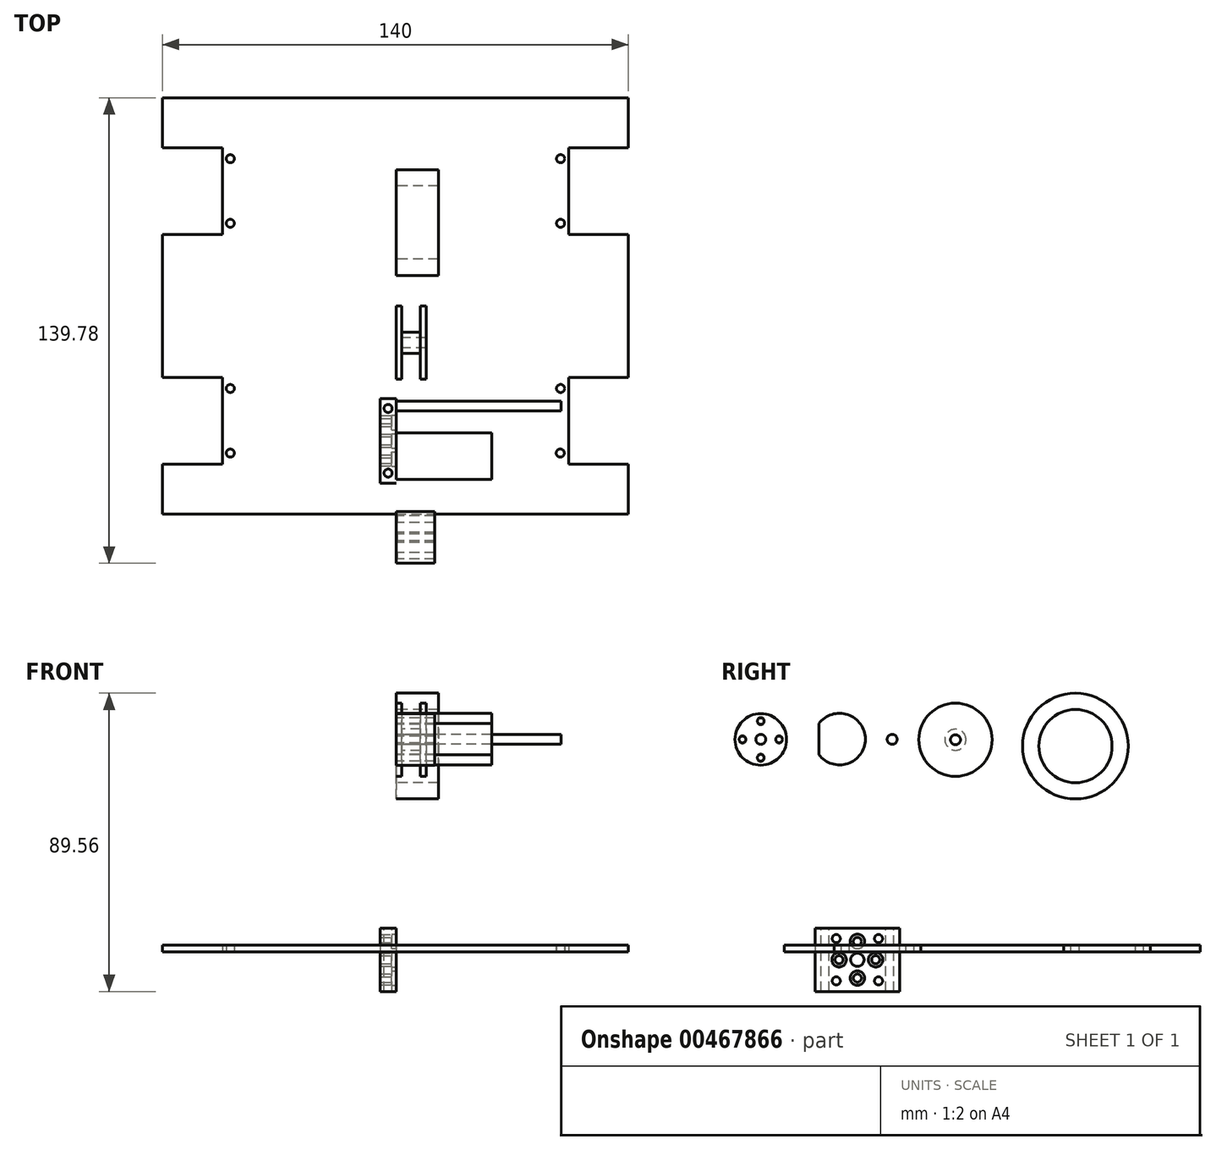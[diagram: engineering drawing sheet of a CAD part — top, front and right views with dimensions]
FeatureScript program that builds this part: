
annotation { "Feature Type Name" : "Feature", "Feature Type Description" : "" }
export const myFeature = defineFeature(function(context is Context, id is Id, definition is map)
    precondition{}
    {
        {
            var Q0;
            Q0=qCreatedBy(makeId("Top.planeOp"),FACE);
            var sketch = newSketch(context, id + "F0", { "sketchPlane" : qUnion([Q0])});
            skLineSegment(sketch, "E0.top", {"start": v(69.81, 68.61) * mm, "end": v(-70.19, 68.61) * mm});
            skPoint(sketch, "E0.middle", {"position": v(-0.01, 0) * mm});
            skLineSegment(sketch, "E1", {"start": v(69.81, 53.61) * mm, "end": v(69.81, 68.61) * mm});
            skLineSegment(sketch, "E2", {"start": v(-70.19, 53.61) * mm, "end": v(-52.19, 53.61) * mm});
            skLineSegment(sketch, "E3", {"start": v(-52.19, 27.61) * mm, "end": v(-52.19, 53.61) * mm});
            skLineSegment(sketch, "E4", {"start": v(-70.19, 53.61) * mm, "end": v(-70.19, 68.61) * mm});
            skLineSegment(sketch, "E5", {"start": v(-52.19, 27.61) * mm, "end": v(-70.19, 27.61) * mm});
            skLineSegment(sketch, "E6", {"start": v(-70.19, -56.39) * mm, "end": v(69.81, -56.39) * mm});
            skLineSegment(sketch, "E7", {"start": v(69.81, 53.61) * mm, "end": v(51.81, 53.61) * mm});
            skLineSegment(sketch, "E8", {"start": v(51.81, 53.61) * mm, "end": v(51.81, 27.61) * mm});
            skLineSegment(sketch, "E9", {"start": v(51.81, 27.61) * mm, "end": v(69.81, 27.61) * mm});
            skLineSegment(sketch, "E10", {"start": v(69.81, -56.39) * mm, "end": v(69.81, -41.39) * mm});
            skLineSegment(sketch, "E11", {"start": v(69.81, -41.39) * mm, "end": v(51.81, -41.39) * mm});
            skLineSegment(sketch, "E12", {"start": v(51.81, -41.39) * mm, "end": v(51.81, -15.39) * mm});
            skLineSegment(sketch, "E13", {"start": v(51.81, -15.39) * mm, "end": v(69.81, -15.39) * mm});
            skLineSegment(sketch, "E14", {"start": v(-70.19, -56.39) * mm, "end": v(-70.19, -41.39) * mm});
            skLineSegment(sketch, "E15", {"start": v(-70.19, -41.39) * mm, "end": v(-52.19, -41.39) * mm});
            skLineSegment(sketch, "E16", {"start": v(-52.19, -41.39) * mm, "end": v(-52.19, -15.39) * mm});
            skLineSegment(sketch, "E17", {"start": v(-52.19, -15.39) * mm, "end": v(-70.19, -15.39) * mm});
            skLineSegment(sketch, "E18", {"start": v(-70.19, 27.61) * mm, "end": v(-70.19, -15.39) * mm});
            skLineSegment(sketch, "E19", {"start": v(69.81, 27.61) * mm, "end": v(69.81, -15.39) * mm});
            skCircle(sketch, "E20", {"center": v(-49.8, -18.69) * mm, "radius": 1.22 * mm});
            skCircle(sketch, "E21", {"center": v(-49.8, -38.09) * mm, "radius": 1.22 * mm});
            skCircle(sketch, "E22", {"center": v(49.43, -18.69) * mm, "radius": 1.22 * mm});
            skCircle(sketch, "E23", {"center": v(49.33, -38.09) * mm, "radius": 1.22 * mm});
            skCircle(sketch, "E24", {"center": v(49.43, 50.31) * mm, "radius": 1.22 * mm});
            skCircle(sketch, "E25", {"center": v(49.43, 30.91) * mm, "radius": 1.22 * mm});
            skCircle(sketch, "E26", {"center": v(-49.8, 50.31) * mm, "radius": 1.22 * mm});
            skCircle(sketch, "E27", {"center": v(-49.8, 30.91) * mm, "radius": 1.22 * mm});
            skSolve(sketch);
        }
        {
            var Q0;
            Q0 = qSketchRegion(id + "F0", true);
            extrude(context, id + "F1", {"entities" : qUnion([Q0]), "depth" : 2 * mm});
        }
        {
            var Q0;
            Q0=qCreatedBy(makeId("Right.planeOp"),FACE);
            var sketch = newSketch(context, id + "F2", { "sketchPlane" : qUnion([Q0])});
            skLineSegment(sketch, "E28", {"start": v(-47.09, -11.9) * mm, "end": v(-21.69, -11.9) * mm});
            skLineSegment(sketch, "E29", {"start": v(-21.69, -11.9) * mm, "end": v(-21.69, 7.16) * mm});
            skLineSegment(sketch, "E30", {"start": v(-21.69, 7.16) * mm, "end": v(-47.09, 7.16) * mm});
            skLineSegment(sketch, "E31", {"start": v(-47.09, 7.16) * mm, "end": v(-47.09, -11.9) * mm});
            skCircle(sketch, "E32", {"center": v(-40.74, 3.98) * mm, "radius": 1.22 * mm});
            skCircle(sketch, "E33", {"center": v(-28.04, 3.98) * mm, "radius": 1.22 * mm});
            skCircle(sketch, "E34", {"center": v(-40.74, -8.72) * mm, "radius": 1.22 * mm});
            skCircle(sketch, "E35", {"center": v(-28.04, -8.72) * mm, "radius": 1.22 * mm});
            skCircle(sketch, "E36", {"center": v(-34.39, -2.37) * mm, "radius": 2 * mm});
            skCircle(sketch, "E37", {"center": v(-39.89, -2.37) * mm, "radius": 1.22 * mm});
            skCircle(sketch, "E38", {"center": v(-34.39, 3.13) * mm, "radius": 1.22 * mm});
            skCircle(sketch, "E39", {"center": v(-28.89, -2.37) * mm, "radius": 1.22 * mm});
            skCircle(sketch, "E40", {"center": v(-34.39, -7.87) * mm, "radius": 1.22 * mm});
            skCircle(sketch, "E41", {"center": v(-28.04, 3.98) * mm, "radius": 2.17 * mm});
            skCircle(sketch, "E42", {"center": v(-40.74, 3.98) * mm, "radius": 2.17 * mm});
            skCircle(sketch, "E43", {"center": v(-40.74, -8.72) * mm, "radius": 2.17 * mm});
            skCircle(sketch, "E44", {"center": v(-28.04, -8.72) * mm, "radius": 2.17 * mm});
            skSolve(sketch);
        }
        {
            var Q0;
            Q0=makeQuery(id+"F2.imprint","IMPRINT",FACE,{"disambiguationData":[TD([[makeQuery(id+"F2.imprint","IMPRINT",EDGE,{"derivedFrom":sQuery(id+"F2.wireOp",EDGE,"E32")}),-1.0]])]});
            var Q1;
            Q1=makeQuery(id+"F2.imprint","IMPRINT",FACE,{"disambiguationData":[TD([[makeQuery(id+"F2.imprint","IMPRINT",EDGE,{"derivedFrom":sQuery(id+"F2.wireOp",EDGE,"E33")}),-1.0]])]});
            var Q2;
            Q2=makeQuery(id+"F2.imprint","IMPRINT",FACE,{"disambiguationData":[TD([[makeQuery(id+"F2.imprint","IMPRINT",EDGE,{"derivedFrom":sQuery(id+"F2.wireOp",EDGE,"E34")}),-1.0]])]});
            var Q3;
            Q3=makeQuery(id+"F2.imprint","IMPRINT",FACE,{"disambiguationData":[TD([[makeQuery(id+"F2.imprint","IMPRINT",EDGE,{"derivedFrom":sQuery(id+"F2.wireOp",EDGE,"E35")}),-1.0]])]});
            var Q4;
            Q4=makeQuery(id+"F2.imprint","IMPRINT",FACE,{"disambiguationData":[TD([[makeQuery(id+"F2.imprint","IMPRINT",EDGE,{"derivedFrom":sQuery(id+"F2.wireOp",EDGE,"E28")}),1.0]])]});
            extrude(context, id + "F3", {"entities" : qUnion([Q0, Q1, Q2, Q3, Q4]), "oppositeDirection" : true, "depth" : 4.76 * mm});
        }
        {
            var Q0;
            Q0=sQuery(id+"F2.wireOp",VERTEX,"E37.center");
            var Q1;
            Q1=sQuery(id+"F2.wireOp",VERTEX,"E38.center");
            var Q2;
            Q2=sQuery(id+"F2.wireOp",VERTEX,"E39.center");
            var Q3;
            Q3=sQuery(id+"F2.wireOp",VERTEX,"E40.center");
            var Q4;
            Q4=makeQuery(id+"F3.opExtrude","SWEPT_BODY",BODY,{"disambiguationData":[OSD([sQuery(id+"F2.wireOp",EDGE,"E28"),sQuery(id+"F2.wireOp",EDGE,"E29"),sQuery(id+"F2.wireOp",EDGE,"E30"),sQuery(id+"F2.wireOp",EDGE,"E31"),sQuery(id+"F2.wireOp",EDGE,"E32"),sQuery(id+"F2.wireOp",EDGE,"E33"),sQuery(id+"F2.wireOp",EDGE,"E34"),sQuery(id+"F2.wireOp",EDGE,"E35"),sQuery(id+"F2.wireOp",EDGE,"E36"),sQuery(id+"F2.wireOp",EDGE,"E37"),sQuery(id+"F2.wireOp",EDGE,"E38"),sQuery(id+"F2.wireOp",EDGE,"E39"),sQuery(id+"F2.wireOp",EDGE,"E40")])]});
            hole(context, id + "F4", {"style" : HoleStyle.C_BORE, "endStyle" : HoleEndStyle.THROUGH, "holeDiameter" : 2.44 * mm, "cBoreDiameter" : 4.35 * mm, "cBoreDepth" : 1.3 * mm, "isTappedThrough" : true, "tappedDepth" : 12 * mm, "tapClearance" : 3, "startFromSketch" : true, "locations" : qUnion([Q0, Q1, Q2, Q3]), "scope" : qUnion([Q4])});
        }
        {
            var Q0;
            Q0=makeQuery(id+"F3.opExtrude","SWEPT_FACE",FACE,{"disambiguationData":[OSD([sQuery(id+"F2.wireOp",EDGE,"E30")])]});
            var sketch = newSketch(context, id + "F5", { "sketchPlane" : qUnion([Q0])});
            skLineSegment(sketch, "E45", {"start": v(-2.38, -34.39) * mm, "end": v(-4.76, -34.39) * mm});
            skPoint(sketch, "E45.startSnap0", {"position": v(-2.38, -34.39) * mm});
            skPoint(sketch, "E45.startSnap1", {"position": v(-2.38, -34.39) * mm});
            skLineSegment(sketch, "E46", {"start": v(-2.38, -34.39) * mm, "end": v(0, -34.39) * mm});
            skLineSegment(sketch, "E47", {"start": v(-2.38, -34.39) * mm, "end": v(-2.38, -44.09) * mm});
            skLineSegment(sketch, "E48", {"start": v(-2.38, -34.39) * mm, "end": v(-2.38, -24.69) * mm});
            skCircle(sketch, "E49", {"center": v(-2.38, -44.09) * mm, "radius": 1.22 * mm});
            skCircle(sketch, "E50", {"center": v(-2.38, -24.69) * mm, "radius": 1219 * mm});
            skCircle(sketch, "E51", {"center": v(-2.38, -24.69) * mm, "radius": 1.22 * mm});
            skSolve(sketch);
        }
        {
            var Q0;
            Q0=sQuery(id+"F5.wireOp",VERTEX,"E49.center");
            var Q1;
            Q1=sQuery(id+"F5.wireOp",VERTEX,"E51.center");
            var Q2;
            Q2=makeQuery(id+"F3.opExtrude","SWEPT_BODY",BODY,{"disambiguationData":[OSD([sQuery(id+"F2.wireOp",EDGE,"E28"),sQuery(id+"F2.wireOp",EDGE,"E29"),sQuery(id+"F2.wireOp",EDGE,"E30"),sQuery(id+"F2.wireOp",EDGE,"E31"),sQuery(id+"F2.wireOp",EDGE,"E32"),sQuery(id+"F2.wireOp",EDGE,"E33"),sQuery(id+"F2.wireOp",EDGE,"E34"),sQuery(id+"F2.wireOp",EDGE,"E35"),sQuery(id+"F2.wireOp",EDGE,"E36"),sQuery(id+"F2.wireOp",EDGE,"E37"),sQuery(id+"F2.wireOp",EDGE,"E38"),sQuery(id+"F2.wireOp",EDGE,"E39"),sQuery(id+"F2.wireOp",EDGE,"E40")])]});
            hole(context, id + "F6", {"style" : HoleStyle.SIMPLE, "endStyle" : HoleEndStyle.THROUGH, "holeDiameter" : 2.44 * mm, "isTappedThrough" : true, "tappedDepth" : 12 * mm, "tapClearance" : 3, "locations" : qUnion([Q0, Q1]), "scope" : qUnion([Q2])});
        }
        {
            var Q0;
            Q0=qCreatedBy(makeId("Right.planeOp"),FACE);
            var sketch = newSketch(context, id + "F7", { "sketchPlane" : qUnion([Q0])});
            skCircle(sketch, "E52", {"center": v(-63.42, 63.79) * mm, "radius": 7.75 * mm});
            skCircle(sketch, "E53", {"center": v(-63.42, 69.29) * mm, "radius": 1 * mm});
            skCircle(sketch, "E54", {"center": v(-68.92, 63.79) * mm, "radius": 1 * mm});
            skCircle(sketch, "E55", {"center": v(-63.42, 58.29) * mm, "radius": 1 * mm});
            skCircle(sketch, "E56", {"center": v(-57.92, 63.79) * mm, "radius": 1 * mm});
            skCircle(sketch, "E57", {"center": v(-63.42, 63.79) * mm, "radius": 1.5 * mm});
            skSolve(sketch);
        }
        {
            var Q0;
            Q0=makeQuery(id+"F7.imprint","IMPRINT",FACE,{"disambiguationData":[TD([[makeQuery(id+"F7.imprint","IMPRINT",EDGE,{"derivedFrom":sQuery(id+"F7.wireOp",EDGE,"E52")}),1.0]])]});
            extrude(context, id + "F8", {"entities" : qUnion([Q0]), "depth" : 11.6 * mm});
        }
        {
            var Q0;
            Q0=makeQuery(id+"F8.opExtrude","CAP_EDGE",EDGE,{"disambiguationData":[OSD([sQuery(id+"F7.wireOp",EDGE,"E53")])],"isStart":true});
            var Q1;
            Q1=makeQuery(id+"F8.opExtrude","CAP_EDGE",EDGE,{"disambiguationData":[OSD([sQuery(id+"F7.wireOp",EDGE,"E56")])],"isStart":true});
            var Q2;
            Q2=makeQuery(id+"F8.opExtrude","CAP_EDGE",EDGE,{"disambiguationData":[OSD([sQuery(id+"F7.wireOp",EDGE,"E54")])],"isStart":true});
            var Q3;
            Q3=makeQuery(id+"F8.opExtrude","CAP_EDGE",EDGE,{"disambiguationData":[OSD([sQuery(id+"F7.wireOp",EDGE,"E55")])],"isStart":true});
            chamfer(context, id + "F9", {"entities" : qUnion([Q0, Q1, Q2, Q3]), "width" : .25 * mm, "tangentPropagation" : true});
        }
        {
            var Q0;
            Q0=qCreatedBy(makeId("Right.planeOp"),FACE);
            var sketch = newSketch(context, id + "F10", { "sketchPlane" : qUnion([Q0])});
            skCircle(sketch, "E58", {"center": v(-39.75, 63.89) * mm, "radius": 7.75 * mm});
            skLineSegment(sketch, "E59", {"start": v(-45.93, 68.56) * mm, "end": v(-45.93, 59.21) * mm});
            skSolve(sketch);
        }
        {
            var Q0;
            {var subQ0=sQuery(id+"F10.wireOp",EDGE,"E59");Q0=makeQuery(id+"F10.imprint","IMPRINT",FACE,{"disambiguationData":[TD([[makeQuery(id+"F10.imprint","IMPRINT",EDGE,{"derivedFrom":subQ0}),1.0]])]});}
            extrude(context, id + "F11", {"entities" : qUnion([Q0]), "depth" : 28.7 * mm});
        }
        {
            var Q0;
            Q0=qCreatedBy(makeId("Right.planeOp"),FACE);
            var sketch = newSketch(context, id + "F12", { "sketchPlane" : qUnion([Q0])});
            skCircle(sketch, "E60", {"center": v(-23.94, 63.8) * mm, "radius": 1.5 * mm});
            skSolve(sketch);
        }
        {
            var Q0;
            Q0 = qSketchRegion(id + "F12", true);
            extrude(context, id + "F13", {"entities" : qUnion([Q0]), "depth" : 49.6 * mm});
        }
        {
            var Q0;
            Q0=qCreatedBy(makeId("Right.planeOp"),FACE);
            var sketch = newSketch(context, id + "F14", { "sketchPlane" : qUnion([Q0])});
            skCircle(sketch, "E61", {"center": v(-4.92, 63.7) * mm, "radius": 11 * mm});
            skCircle(sketch, "E62", {"center": v(-4.92, 63.7) * mm, "radius": 1.5 * mm});
            skSolve(sketch);
        }
        {
            var Q0;
            Q0=makeQuery(id+"F14.imprint","IMPRINT",FACE,{"disambiguationData":[TD([[makeQuery(id+"F14.imprint","IMPRINT",EDGE,{"derivedFrom":sQuery(id+"F14.wireOp",EDGE,"E61")}),1.0]])]});
            extrude(context, id + "F15", {"entities" : qUnion([Q0]), "depth" : 9 * mm});
        }
        {
            var Q0;
            Q0=makeQuery(id+"F15.opExtrude","SWEPT_FACE",FACE,{"disambiguationData":[OSD([sQuery(id+"F14.wireOp",EDGE,"E61")])]});
            shell(context, id + "F16", {"entities" : qUnion([Q0]), "thickness" : 1.68 * mm});
        }
        {
            var Q0;
            Q0=qCreatedBy(makeId("Right.planeOp"),FACE);
            var sketch = newSketch(context, id + "F17", { "sketchPlane" : qUnion([Q0])});
            skCircle(sketch, "E63", {"center": v(31.13, 61.8) * mm, "radius": 15.88 * mm});
            skCircle(sketch, "E64", {"center": v(31.13, 61.8) * mm, "radius": 3.18 * mm});
            skCircle(sketch, "E65", {"center": v(31.13, 61.8) * mm, "radius": 11 * mm});
            skSolve(sketch);
        }
        {
            var Q0;
            Q0 = qSketchRegion(id + "F17", true);
            var Q1;
            Q1=makeQuery(id+"F17.imprint","IMPRINT",FACE,{"disambiguationData":[TD([[makeQuery(id+"F17.imprint","IMPRINT",EDGE,{"derivedFrom":sQuery(id+"F17.wireOp",EDGE,"E64")}),-1.0]])]});
            extrude(context, id + "F18", {"entities" : qUnion([Q0, Q1]), "depth" : 12.7 * mm});
        }
        {
            var Q0;
            Q0=sQuery(id+"F17.wireOp",VERTEX,"E65.center");
            var Q1;
            Q1=makeQuery(id+"F18.opExtrude","SWEPT_BODY",BODY,{"disambiguationData":[OSD([sQuery(id+"F17.wireOp",EDGE,"E63"),sQuery(id+"F17.wireOp",EDGE,"E64")])]});
            hole(context, id + "F19", {"style" : HoleStyle.SIMPLE, "endStyle" : HoleEndStyle.BLIND, "oppositeDirection" : true, "holeDiameter" : 22 * mm, "holeDepth" : 20 * mm, "isTappedThrough" : true, "tappedDepth" : 12 * mm, "tapClearance" : 3, "locations" : qUnion([Q0]), "scope" : qUnion([Q1])});
        }
    });
